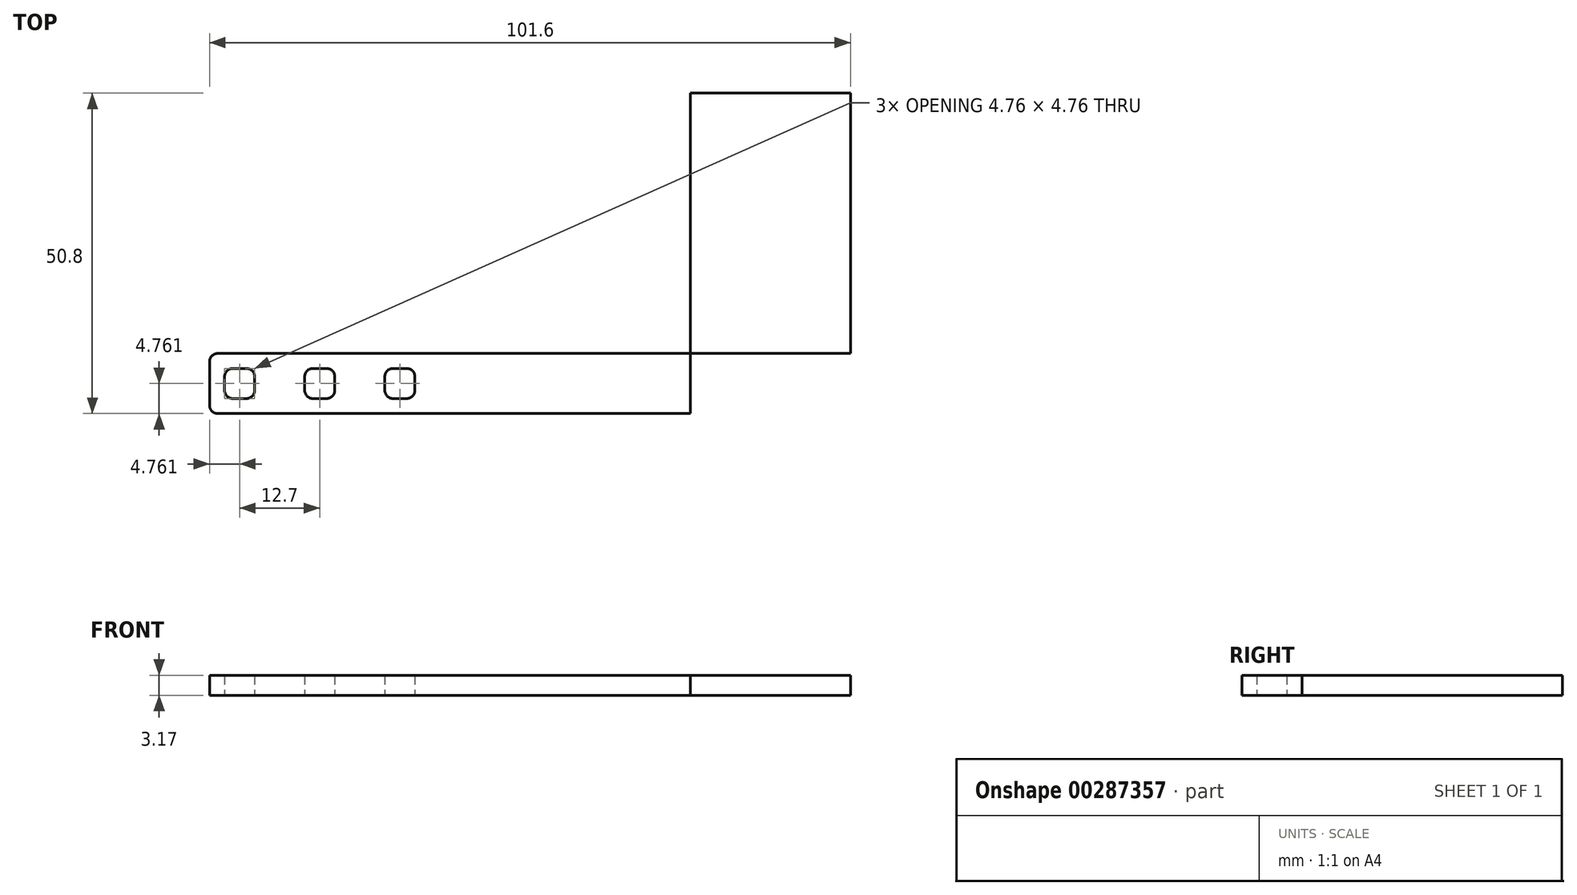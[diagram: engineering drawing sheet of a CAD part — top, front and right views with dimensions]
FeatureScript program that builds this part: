
annotation { "Feature Type Name" : "Feature", "Feature Type Description" : "" }
export const myFeature = defineFeature(function(context is Context, id is Id, definition is map)
    precondition{}
    {
        {
            var Q0;
            Q0=qCreatedBy(makeId("Top.planeOp"),FACE);
            var sketch = newSketch(context, id + "F0", { "sketchPlane" : qUnion([Q0])});
            skLineSegment(sketch, "E0.bottom", {"start": v(0, 0) * mm, "end": v(4.76, 0) * mm});
            skLineSegment(sketch, "E0.top", {"start": v(0, 4.76) * mm, "end": v(4.76, 4.76) * mm});
            skLineSegment(sketch, "E0.left", {"start": v(0, 0) * mm, "end": v(0, 4.76) * mm});
            skLineSegment(sketch, "E0.right", {"start": v(4.76, 0) * mm, "end": v(4.76, 4.76) * mm});
            skLineSegment(sketch, "E1.1.0.0", {"start": v(17.46, 0) * mm, "end": v(17.46, 4.76) * mm});
            skLineSegment(sketch, "E1.1.0.1", {"start": v(12.7, 0) * mm, "end": v(12.7, 4.76) * mm});
            skLineSegment(sketch, "E1.1.0.2", {"start": v(12.7, 4.76) * mm, "end": v(17.46, 4.76) * mm});
            skLineSegment(sketch, "E1.1.0.3", {"start": v(12.7, 0) * mm, "end": v(17.46, 0) * mm});
            skLineSegment(sketch, "E1.2.0.0", {"start": v(30.16, 0) * mm, "end": v(30.16, 4.76) * mm});
            skLineSegment(sketch, "E1.2.0.1", {"start": v(25.4, 0) * mm, "end": v(25.4, 4.76) * mm});
            skLineSegment(sketch, "E1.2.0.2", {"start": v(25.4, 4.76) * mm, "end": v(30.16, 4.76) * mm});
            skLineSegment(sketch, "E1.2.0.3", {"start": v(25.4, 0) * mm, "end": v(30.16, 0) * mm});
            skLineSegment(sketch, "E1.direction1", {"start": v(0, 0) * mm, "end": v(12.7, 0) * mm, "construction": true});
            skLineSegment(sketch, "E2", {"start": v(2.38, 2.38) * mm, "end": v(2.38, 7.14) * mm, "construction": true});
            skPoint(sketch, "E2.startSnap0", {"position": v(2.38, 0) * mm});
            skPoint(sketch, "E2.startSnap1", {"position": v(0, 2.38) * mm});
            skPoint(sketch, "E2.endSnap0", {"position": v(2.38, 4.76) * mm});
            skLineSegment(sketch, "E3", {"start": v(2.38, 7.14) * mm, "end": v(-2.38, 7.14) * mm, "construction": true});
            skLineSegment(sketch, "E4.bottom", {"start": v(-2.38, 7.14) * mm, "end": v(99.22, 7.14) * mm});
            skLineSegment(sketch, "E4.top", {"start": v(-2.38, -2.38) * mm, "end": v(99.22, -2.38) * mm});
            skLineSegment(sketch, "E4.left", {"start": v(-2.38, 7.14) * mm, "end": v(-2.38, -2.38) * mm});
            skLineSegment(sketch, "E4.right", {"start": v(99.22, 7.14) * mm, "end": v(99.22, -2.38) * mm});
            skLineSegment(sketch, "E5.bottom", {"start": v(99.22, -2.38) * mm, "end": v(73.82, -2.38) * mm});
            skLineSegment(sketch, "E5.top", {"start": v(99.22, 48.42) * mm, "end": v(73.82, 48.42) * mm});
            skLineSegment(sketch, "E5.left", {"start": v(99.22, -2.38) * mm, "end": v(99.22, 48.42) * mm});
            skLineSegment(sketch, "E5.right", {"start": v(73.82, -2.38) * mm, "end": v(73.82, 48.42) * mm});
            skSolve(sketch);
        }
        {
            var Q0;
            {var subQ5=sQuery(id+"F0.wireOp",EDGE,"E5.top");Q0=makeQuery(id+"F0.imprint","IMPRINT",FACE,{"disambiguationData":[TD([[makeQuery(id+"F0.imprint","IMPRINT",EDGE,{"derivedFrom":subQ5}),1.0]])]});}
            var Q1;
            {var subQ5=sQuery(id+"F0.wireOp",EDGE,"E5.bottom");Q1=makeQuery(id+"F0.imprint","IMPRINT",FACE,{"disambiguationData":[TD([[makeQuery(id+"F0.imprint","IMPRINT",EDGE,{"derivedFrom":subQ5}),-1.0]])]});}
            var Q2;
            Q2=makeQuery(id+"F0.imprint","IMPRINT",FACE,{"disambiguationData":[TD([[makeQuery(id+"F0.imprint","IMPRINT",EDGE,{"derivedFrom":sQuery(id+"F0.wireOp",EDGE,"E0.bottom")}),-1.0]])]});
            extrude(context, id + "F1", {"entities" : qUnion([Q0, Q1, Q2]), "depth" : 3.17 * mm});
        }
        {
            var Q0;
            Q0=makeQuery(id+"F1.opExtrude","SWEPT_EDGE",EDGE,{"disambiguationData":[OSD([sQuery(id+"F0.wireOp",EDGE,"E4.top"),sQuery(id+"F0.wireOp",EDGE,"E4.left")])]});
            var Q1;
            Q1=makeQuery(id+"F1.opExtrude","SWEPT_EDGE",EDGE,{"disambiguationData":[OSD([sQuery(id+"F0.wireOp",EDGE,"E0.top"),sQuery(id+"F0.wireOp",EDGE,"E0.left")])]});
            var Q2;
            Q2=makeQuery(id+"F1.opExtrude","SWEPT_EDGE",EDGE,{"disambiguationData":[OSD([sQuery(id+"F0.wireOp",EDGE,"E1.1.0.1"),sQuery(id+"F0.wireOp",EDGE,"E1.1.0.2")])]});
            var Q3;
            Q3=makeQuery(id+"F1.opExtrude","SWEPT_EDGE",EDGE,{"disambiguationData":[OSD([sQuery(id+"F0.wireOp",EDGE,"E1.2.0.1"),sQuery(id+"F0.wireOp",EDGE,"E1.2.0.2")])]});
            var Q4;
            Q4=makeQuery(id+"F1.opExtrude","SWEPT_EDGE",EDGE,{"disambiguationData":[OSD([sQuery(id+"F0.wireOp",EDGE,"E4.bottom"),sQuery(id+"F0.wireOp",EDGE,"E4.left")])]});
            var Q5;
            Q5=makeQuery(id+"F1.opExtrude","SWEPT_EDGE",EDGE,{"disambiguationData":[OSD([sQuery(id+"F0.wireOp",EDGE,"E0.bottom"),sQuery(id+"F0.wireOp",EDGE,"E0.left")])]});
            var Q6;
            Q6=makeQuery(id+"F1.opExtrude","SWEPT_EDGE",EDGE,{"disambiguationData":[OSD([sQuery(id+"F0.wireOp",EDGE,"E1.1.0.1"),sQuery(id+"F0.wireOp",EDGE,"E1.1.0.3")])]});
            var Q7;
            Q7=makeQuery(id+"F1.opExtrude","SWEPT_EDGE",EDGE,{"disambiguationData":[OSD([sQuery(id+"F0.wireOp",EDGE,"E1.2.0.1"),sQuery(id+"F0.wireOp",EDGE,"E1.2.0.3")])]});
            var Q8;
            Q8=makeQuery(id+"F1.opExtrude","SWEPT_EDGE",EDGE,{"disambiguationData":[OSD([sQuery(id+"F0.wireOp",EDGE,"E0.bottom"),sQuery(id+"F0.wireOp",EDGE,"E0.right")])]});
            var Q9;
            Q9=makeQuery(id+"F1.opExtrude","SWEPT_EDGE",EDGE,{"disambiguationData":[OSD([sQuery(id+"F0.wireOp",EDGE,"E1.1.0.0"),sQuery(id+"F0.wireOp",EDGE,"E1.1.0.3")])]});
            var Q10;
            Q10=makeQuery(id+"F1.opExtrude","SWEPT_EDGE",EDGE,{"disambiguationData":[OSD([sQuery(id+"F0.wireOp",EDGE,"E1.2.0.0"),sQuery(id+"F0.wireOp",EDGE,"E1.2.0.3")])]});
            var Q11;
            Q11=makeQuery(id+"F1.opExtrude","SWEPT_EDGE",EDGE,{"disambiguationData":[OSD([sQuery(id+"F0.wireOp",EDGE,"E0.top"),sQuery(id+"F0.wireOp",EDGE,"E0.right")])]});
            var Q12;
            Q12=makeQuery(id+"F1.opExtrude","SWEPT_EDGE",EDGE,{"disambiguationData":[OSD([sQuery(id+"F0.wireOp",EDGE,"E1.1.0.0"),sQuery(id+"F0.wireOp",EDGE,"E1.1.0.2")])]});
            var Q13;
            Q13=makeQuery(id+"F1.opExtrude","SWEPT_EDGE",EDGE,{"disambiguationData":[OSD([sQuery(id+"F0.wireOp",EDGE,"E1.2.0.0"),sQuery(id+"F0.wireOp",EDGE,"E1.2.0.2")])]});
            fillet(context, id + "F2", {"entities" : qUnion([Q0, Q1, Q2, Q3, Q4, Q5, Q6, Q7, Q8, Q9, Q10, Q11, Q12, Q13]), "radius" : 1.27 * mm, "tangentPropagation" : true, "allowEdgeOverflow" : false});
        }
    });
